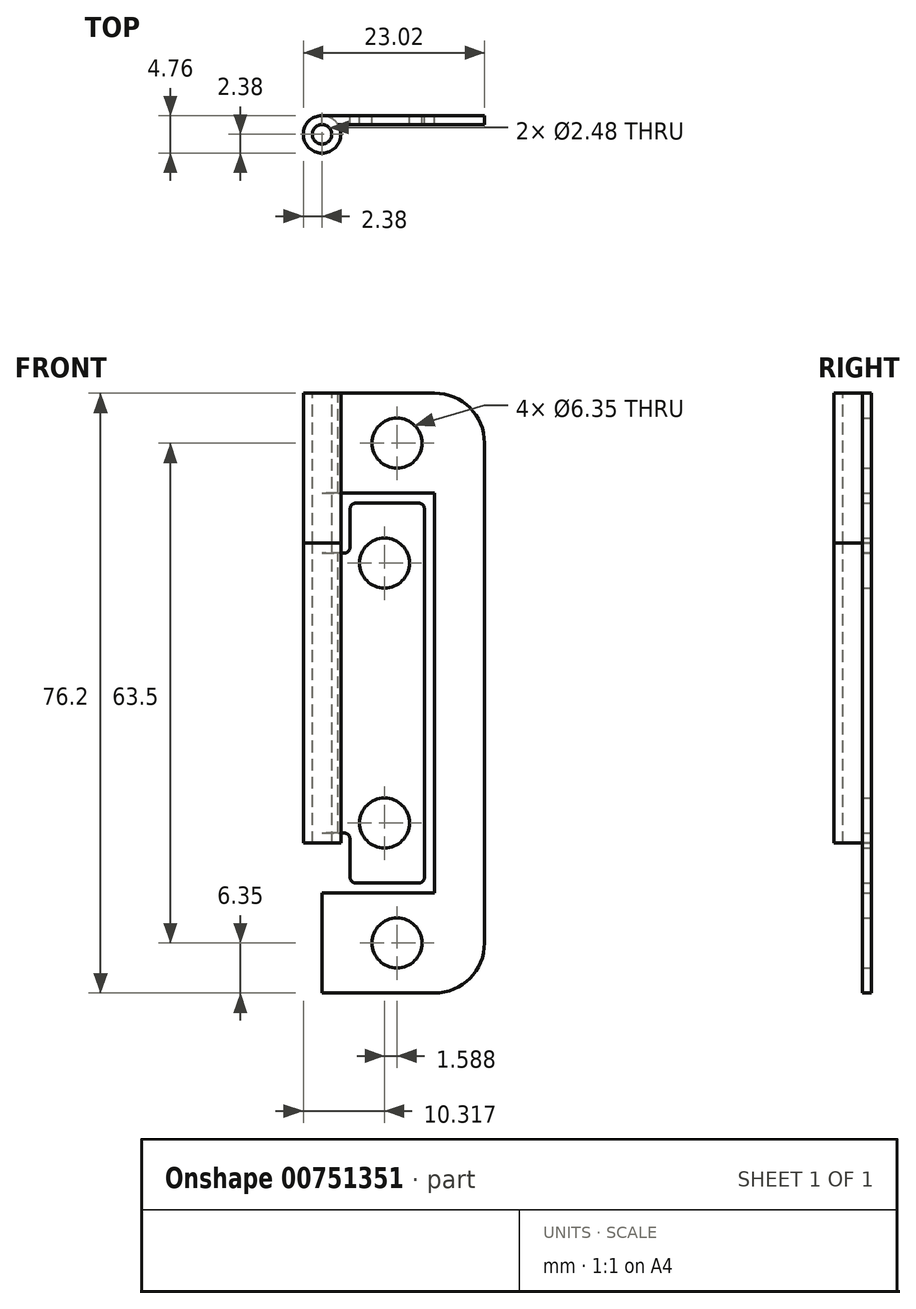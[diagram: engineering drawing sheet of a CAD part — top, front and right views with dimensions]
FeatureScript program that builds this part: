
annotation { "Feature Type Name" : "Feature", "Feature Type Description" : "" }
export const myFeature = defineFeature(function(context is Context, id is Id, definition is map)
    precondition{}
    {
        {
            assignVariable(context, id + "F0", {"name" : "hinge_height", "anyValue" : 76.2 * mm});
        }
        {
            var Q0;
            Q0=qCreatedBy(makeId("Front.planeOp"),FACE);
            var sketch = newSketch(context, id + "F1", { "sketchPlane" : qUnion([Q0])});
            skLineSegment(sketch, "E0.bottom", {"start": v(0, 0) * mm, "end": v(14.29, 0) * mm});
            skLineSegment(sketch, "E0.top", {"start": v(0, 76.2) * mm, "end": v(14.29, 76.2) * mm});
            skLineSegment(sketch, "E0.left", {"start": v(0, 0) * mm, "end": v(0, 12.7) * mm});
            skLineSegment(sketch, "E0.right", {"start": v(20.64, 6.35) * mm, "end": v(20.64, 69.85) * mm});
            skPoint(sketch, "E1.visualSharp", {"position": v(20.64, 76.2) * mm});
            skArc(sketch, "E1.filletArc", {"start": v(20.64, 69.85) * mm, "mid": v(18.78, 74.34) * mm, "end": v(14.29, 76.2) * mm});
            skPoint(sketch, "E2.visualSharp", {"position": v(20.64, 0) * mm});
            skArc(sketch, "E2.filletArc", {"start": v(14.29, 0) * mm, "mid": v(18.78, 1.86) * mm, "end": v(20.64, 6.35) * mm});
            skLineSegment(sketch, "E3.bottom", {"start": v(0, 63.5) * mm, "end": v(14.29, 63.5) * mm});
            skLineSegment(sketch, "E3.top", {"start": v(0, 12.7) * mm, "end": v(14.29, 12.7) * mm});
            skLineSegment(sketch, "E3.right", {"start": v(14.29, 63.5) * mm, "end": v(14.29, 12.7) * mm});
            skLineSegment(sketch, "E4.trimOffspring", {"start": v(0, 63.5) * mm, "end": v(0, 76.2) * mm});
            skCircle(sketch, "E5", {"center": v(9.53, 69.85) * mm, "radius": 3.18 * mm});
            skLineSegment(sketch, "E6", {"start": v(9.53, 76.2) * mm, "end": v(9.53, 63.5) * mm, "construction": true});
            skCircle(sketch, "E7.MirrorC", {"center": v(9.53, 6.35) * mm, "radius": 3.18 * mm});
            skLineSegment(sketch, "E8", {"start": v(9.53, 6.35) * mm, "end": v(9.53, 12.7) * mm, "construction": true});
            skLineSegment(sketch, "E9", {"start": v(9.53, 6.35) * mm, "end": v(9.53, 0) * mm, "construction": true});
            skSolve(sketch);
        }
        {
            var Q0;
            Q0 = qSketchRegion(id + "F1", true);
            extrude(context, id + "F2", {"entities" : qUnion([Q0]), "endBound" : BoundingType.SYMMETRIC, "depth" : 1.14 * mm, "offsetDistance" : 25.4 * mm});
        }
        {
            var Q0;
            Q0=makeQuery(id+"F2.opExtrude","SWEPT_FACE",FACE,{"disambiguationData":[OSD([sQuery(id+"F1.wireOp",EDGE,"E0.top")])]});
            var sketch = newSketch(context, id + "F3", { "sketchPlane" : qUnion([Q0])});
            skCircle(sketch, "E10", {"center": v(0, -1.8) * mm, "radius": 2.38 * mm});
            skCircle(sketch, "E11", {"center": v(0, -1.8) * mm, "radius": 1.24 * mm});
            skSolve(sketch);
        }
        {
            var Q0;
            Q0 = qSketchRegion(id + "F3", true);
            extrude(context, id + "F4", {"entities" : qUnion([Q0]), "operationType" : NewBodyOperationType.ADD, "oppositeDirection" : true, "depth" : 19.05 * mm, "offsetDistance" : 25.4 * mm});
        }
        {
            var Q0;
            Q0=qCreatedBy(makeId("Top.planeOp"),FACE);
            cPlane(context, id + "F5", {"entities" : qUnion([Q0]), "cplaneType" : CPlaneType.OFFSET, "offset" : getVariable(context, 'hinge_height') / 2, "width" : 152.4 * mm, "height" : 152.4 * mm});
        }
        {
            var Q0;
            Q0=makeQuery(id+"F4.opExtrude","CAP_FACE",FACE,{"disambiguationData":[OSD([sQuery(id+"F3.wireOp",EDGE,"E10"),sQuery(id+"F3.wireOp",EDGE,"E11")])],"isStart":false});
            var sketch = newSketch(context, id + "F6", { "sketchPlane" : qUnion([Q0])});
            skCircle(sketch, "E12.0", {"center": v(0, 1.8) * mm, "radius": 1.24 * mm});
            skCircle(sketch, "E13.0", {"center": v(0, 1.8) * mm, "radius": 2.38 * mm});
            skSolve(sketch);
        }
        {
            var Q0;
            Q0 = qSketchRegion(id + "F6", true);
            extrude(context, id + "F7", {"entities" : qUnion([Q0]), "depth" : 38.1 * mm, "offsetDistance" : 25.4 * mm});
        }
        {
            var Q0;
            Q0=qCreatedBy(makeId("Front.planeOp"),FACE);
            var sketch = newSketch(context, id + "F8", { "sketchPlane" : qUnion([Q0])});
            skLineSegment(sketch, "E14.bottom", {"start": v(4.32, 62.23) * mm, "end": v(12.26, 62.23) * mm});
            skLineSegment(sketch, "E14.top", {"start": v(4.32, 13.97) * mm, "end": v(12.26, 13.97) * mm});
            skLineSegment(sketch, "E14.left", {"start": v(3.56, 61.47) * mm, "end": v(3.56, 56.64) * mm});
            skLineSegment(sketch, "E14.right", {"start": v(13.02, 61.47) * mm, "end": v(13.02, 14.73) * mm});
            skLineSegment(sketch, "E15", {"start": v(2.8, 55.88) * mm, "end": v(0, 55.88) * mm});
            skLineSegment(sketch, "E16", {"start": v(0, 55.88) * mm, "end": v(0, 20.32) * mm});
            skLineSegment(sketch, "E17", {"start": v(0, 20.32) * mm, "end": v(2.8, 20.32) * mm});
            skLineSegment(sketch, "E18.trimOffspring", {"start": v(3.56, 19.56) * mm, "end": v(3.56, 14.73) * mm});
            skPoint(sketch, "E19.visualSharp", {"position": v(3.56, 55.88) * mm});
            skArc(sketch, "E19.filletArc", {"start": v(2.8, 55.88) * mm, "mid": v(3.33, 56.1) * mm, "end": v(3.56, 56.64) * mm});
            skPoint(sketch, "E20.visualSharp", {"position": v(3.56, 20.32) * mm});
            skArc(sketch, "E20.filletArc", {"start": v(3.56, 19.56) * mm, "mid": v(3.33, 20.1) * mm, "end": v(2.8, 20.32) * mm});
            skCircle(sketch, "E21", {"center": v(7.94, 54.61) * mm, "radius": 3.18 * mm});
            skCircle(sketch, "E22", {"center": v(7.94, 21.6) * mm, "radius": 3.18 * mm});
            skPoint(sketch, "E23.visualSharp", {"position": v(13.02, 62.23) * mm});
            skArc(sketch, "E23.filletArc", {"start": v(13.02, 61.47) * mm, "mid": v(12.8, 62) * mm, "end": v(12.26, 62.23) * mm});
            skPoint(sketch, "E24.visualSharp", {"position": v(13.02, 13.97) * mm});
            skArc(sketch, "E24.filletArc", {"start": v(12.26, 13.97) * mm, "mid": v(12.8, 14.2) * mm, "end": v(13.02, 14.73) * mm});
            skPoint(sketch, "E25.visualSharp", {"position": v(3.56, 13.97) * mm});
            skArc(sketch, "E25.filletArc", {"start": v(3.56, 14.73) * mm, "mid": v(3.78, 14.2) * mm, "end": v(4.32, 13.97) * mm});
            skPoint(sketch, "E26.visualSharp", {"position": v(3.56, 62.23) * mm});
            skArc(sketch, "E26.filletArc", {"start": v(4.32, 62.23) * mm, "mid": v(3.78, 62) * mm, "end": v(3.56, 61.47) * mm});
            skLineSegment(sketch, "E27", {"start": v(7.94, 62.23) * mm, "end": v(7.94, 54.61) * mm, "construction": true});
            skLineSegment(sketch, "E28", {"start": v(7.94, 21.6) * mm, "end": v(7.94, 13.97) * mm, "construction": true});
            skSolve(sketch);
        }
        {
            var Q0;
            Q0 = qSketchRegion(id + "F8", true);
            extrude(context, id + "F9", {"entities" : qUnion([Q0]), "operationType" : NewBodyOperationType.ADD, "endBound" : BoundingType.SYMMETRIC, "depth" : 1.14 * mm, "offsetDistance" : 25.4 * mm});
        }
    });
